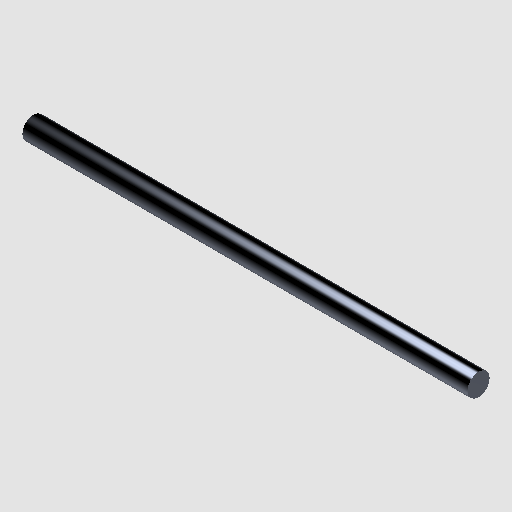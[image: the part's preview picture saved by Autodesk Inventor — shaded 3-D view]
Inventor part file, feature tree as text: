
AUTODESK INVENTOR PART (.ipt)
format: ipt  version: 2024 (Build 280153000, 153)  size: 121,856 bytes
history: native  units: in
note: dims shown in document units (in); Inventor stores cm internally (conversion verified against a paired STEP export)
features: extrude x1, other x1, imported_body x1
ambient origin geometry x8: Origin, YZ Plane, XZ Plane, XY Plane, X Axis, Y Axis, Z Axis, Center Point
bodies: Body1 (feature_tree)
feature tree (3):
  extrude  "Extrude1"  [1 undecoded]
  other  "Pin"
  imported_body  "Base1"
note: 1 required parameter value undecoded (feature->parameter linkage not recoverable at this tier; creation-order binding heuristic only, values carry confidence <= 0.55)
